# Revit family: 97283
name_source: partatom
category: Plumbing Fixtures
revit_build: Autodesk Revit MEP 2012 (Build: 20110916_2132(x64)
units: mm (PartAtom-declared; Revit-internal decimal feet)

## types (2) — shared parameters
Cold Water Flow = 0 GPM
Date Modified = March 13, 2015
Default Elevation = 48 "
Depth = 4.375 "
Equipment Abbreviation = JSF
Family Version = 1.0
Height = 4.5 "
Hot Water Flow = 0 GPM
Manufacturer = Kohler Company
Model Disclaimer = Contact Kohler Company For More Information
Product Material = Chrome - Kohler - Polished
Product Page URL = http://www.us.kohler.com
URL = http://www.us.kohler.com
Width = 2 "

## per-type parameters (varying)
| type | Description | Model | zz Integer 1 |
| With Grid Drain | July Single-Handle Commercial Bathroom Sink Faucet With Grid Drain | K-97283-4-CP | 1 |
| Without Grid Drain | July Single-Handle Commercial Bathroom Sink Faucet Without Grid Drain | K-97282-4-CP | 2 |

## geometry (parser evidence)
native form markers: Sweep x2
no freeform markers — native parametric forms only
